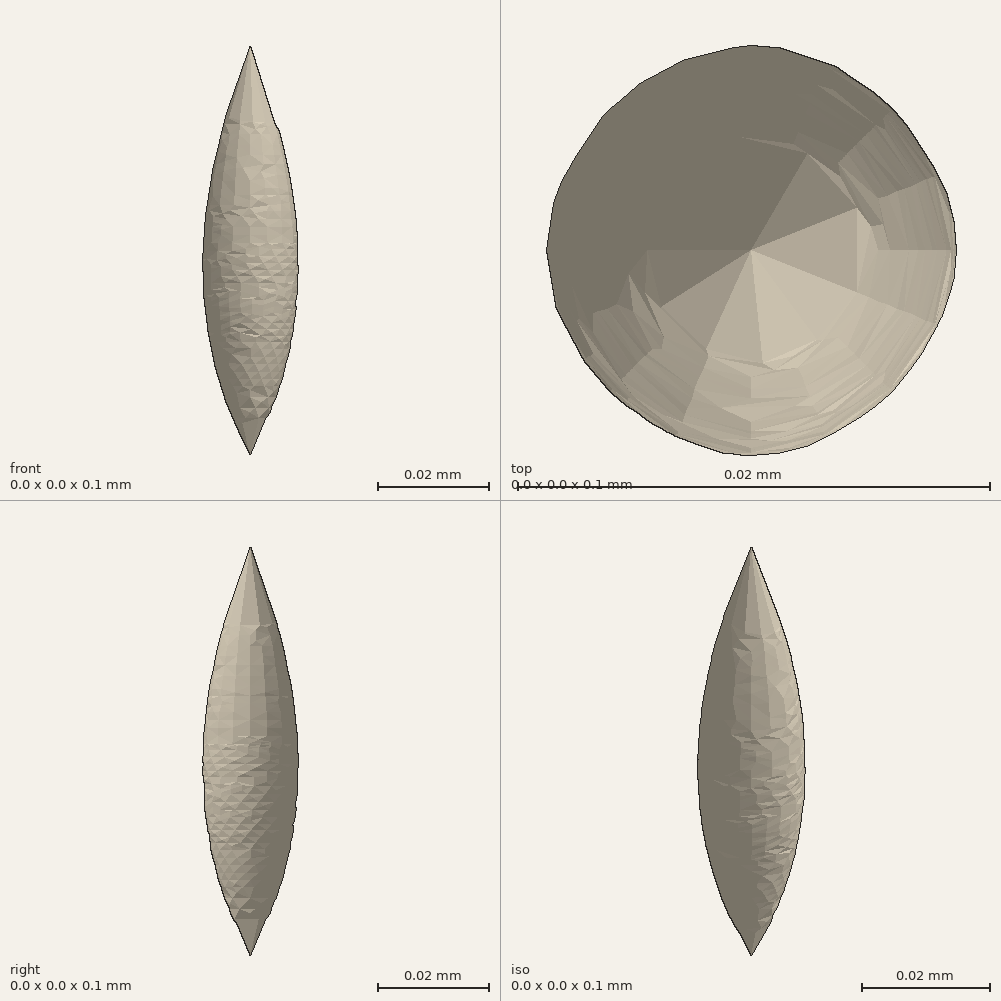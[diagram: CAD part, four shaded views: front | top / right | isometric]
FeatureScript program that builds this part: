
annotation { "Feature Type Name" : "Feature", "Feature Type Description" : "" }
export const myFeature = defineFeature(function(context is Context, id is Id, definition is map)
    precondition{}
    {
        {
            var Q0;
            Q0=qCreatedBy(makeId("Front.planeOp"),FACE);
            var sketch = newSketch(context, id + "F0", { "sketchPlane" : qUnion([Q0])});
            skFitSpline(sketch, "E0", {"points": [v(0, 0) * mm, v(15.72, 2.93) * mm, v(26.07, 3.24) * mm, v(48.6, 0) * mm, v(60.13, 28.67) * mm, v(50.24, 49.54) * mm, v(48.68, 56.64) * mm, v(57.04, 71.06) * mm, v(54.88, 71.06) * mm, v(43.28, 56.64) * mm, v(43.28, 49.54) * mm, v(55.7, 22.62) * mm, v(43.28, 0) * mm, v(26.07, 7.8) * mm, v(14.5, 6.32) * mm, v(0, 0) * mm]});
            skLineSegment(sketch, "E1", {"start": v(0, 73.84) * mm, "end": v(0, -29.13) * mm});
            skSolve(sketch);
        }
        {
            var Q0;
            {var subQ0=sQuery(id+"F0.wireOp",EDGE,"E1");var subQ1=sQuery(id+"F0.wireOp",EDGE,"E0");var subQ2=makeQuery(id+"F0.imprint","INTERSECT",VERTEX,{"disambiguationData":[OD(0.0)],"derivedFrom":[subQ1,subQ0]});Q0=makeQuery(id+"F0.imprint","IMPRINT",FACE,{"disambiguationData":[TD([[makeQuery(id+"F0.imprint","IMPRINT",EDGE,{"disambiguationData":[TD([[subQ2,-1.0]])],"derivedFrom":subQ1}),1.0]])]});}
            var Q1;
            Q1=sQuery(id+"F0.wireOp",EDGE,"E1");
            revolve(context, id + "F1", {"surfaceOperationType" : NewSurfaceOperationType.NEW, "entities" : qUnion([Q0]), "axis" : qUnion([Q1]), "revolveType" : RevolveType.FULL});
        }
        {
            var Q0;
            Q0=qCreatedBy(makeId("Front.planeOp"),FACE);
            var sketch = newSketch(context, id + "F2", { "sketchPlane" : qUnion([Q0])});
            skFitSpline(sketch, "E2", {"points": [v(45.01, 47.32) * mm, v(50.25, 53.8) * mm, v(54.57, 58.42) * mm, v(59.81, 60.58) * mm, v(66.29, 57.5) * mm, v(68.44, 48.87) * mm, v(65.36, 40.85) * mm, v(60.12, 33.76) * mm, v(55.19, 26.36) * mm], "startDerivative": vector(41.79, 51.74) * mm, "endDerivative": vector(-35.67, -56.3) * mm});
            skSolve(sketch);
        }
        {
            var Q0;
            Q0=sQuery(id+"F2.wireOp",VERTEX,"E2.end");
            var Q1;
            Q1=sQuery(id+"F2.wireOp",EDGE,"E2");
            cPlane(context, id + "F3", {"entities" : qUnion([Q0, Q1]), "cplaneType" : CPlaneType.CURVE_POINT, "offset" : 25.4 * mm, "width" : 152.4 * mm, "height" : 152.4 * mm});
        }
    });
